# Revit family: Duncan IP65 temp
name_source: partatom
category: Lighting Fixtures
units: mm (PartAtom-declared; Revit-internal decimal feet)

## family parameters
Always vertical = Yes
Cut with Voids When Loaded = No
Light Source = Yes
OmniClass Number = 23.80.70.11.14
OmniClass Title = General Luminaries, Directional
Part Type = Normal
Room Calculation Point = Yes
Round Connector Dimension = Use Diameter
Shared = No
Work Plane-Based = No

## types (3) — shared parameters
Assembly Code = 63.0
Calc_Length_Luminaire = 1489 mm
Color Filter = 16777215
Dimming Lamp Color Temperature Shift = <None>
Emit Shape Visible in Rendering = No
Emit from Rectangle Length = 60 mm
Emit from Rectangle Width = 1489 mm
IK Value = IK07
IP Value = IP65
IfcExportAs = IfcLightFixtureType
IfcExportType = USERDEFINED
Lamp = LED
Manufacturer = Veko Lightsystems
Model = Duncan IP65
Tilt Angle = 90.00°
URL = https://www.veko.com
⌂ Powered by IVLibrary = www.ivlibrary.com

## per-type parameters (varying)
| type | Apparent Load | Photometric Web File | Wattage Comments |
| Duncan IP65 Lambertian 15m IK07 10030lm 60W 840 | 60 VA | Veko LWDx-L152-07-840-05-nSqiky21bxcr Duncan IP65 Lambertian 15m IK07 10030lm 60W 840_LDT.ies | 59.9W |
| Duncan IP65 Narrow 15m IK07 10003lm 61W 840 | 61 VA | Veko LWDx-N355-07-840-05-nSqiky21bxcr Duncan IP65 Narrow 15m IK07 10003lm 61W 840_LDT.ies | 61W |
| Duncan IP65 Wide 15m IK07 10016lm 62W 840 | 62 VA | Veko LWDx-W355-07-840-05-nSqiky21bxcr Duncan IP65 Wide 15m IK07 10016lm 62W 840_LDT.ies | 62W |

## geometry (parser evidence)
native form markers: Sweep x3
no freeform markers — native parametric forms only
